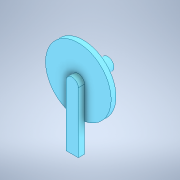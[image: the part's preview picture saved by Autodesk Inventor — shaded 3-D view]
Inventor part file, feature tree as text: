
AUTODESK INVENTOR PART (.ipt)
format: ipt  version: 2020.1 (Build 241239000, 239)  size: 236,032 bytes
history: native  units: in
note: dims shown in document units (in); Inventor stores cm internally (conversion verified against a paired STEP export)
features: extrude x5, sketch x5, projected_geometry x3, plane x1
ambient origin geometry x8: Origin, YZ Plane, XZ Plane, XY Plane, X Axis, Y Axis, Z Axis, Center Point
bodies: Solid1 (feature_tree)
feature tree (14):
  extrude  "Extrusion1"  Depth=0.0787in
  extrude  "Extrusion2"  Depth=0.1969in
  plane  "Work Plane1"
  extrude  "Extrusion7"  TaperAngle=0.0deg  [1 undecoded]
  extrude  "Extrusion8"  Depth=0.0394in
  extrude  "Extrusion10"  TaperAngle=0.0deg  [1 undecoded]
  sketch  "Sketch1"  dims[d0=1.0499in d1=0.0787in]
  sketch  "Sketch2"  dims[d2=0.0in d3=0.1969in]
  sketch  "Sketch5"  dims[d4=0.2756in d5=0.0in]
  projected_geometry  "Projected Loop2"
  sketch  "Sketch6"  dims[d17=-0.0787in d18=0.0394in]
  projected_geometry  "Projected Loop4"
  sketch  "Sketch8"  dims[d19=0.0394in d20=0.0in d23=0.1969in d24=0.1969in d25=0.9706in d27=0.0984in d28=0.0in d32=0.1181in d33=0.0in]
  projected_geometry  "Projected Loop5"
note: 2 required parameter values undecoded (feature->parameter linkage not recoverable at this tier; creation-order binding heuristic only, values carry confidence <= 0.55)
